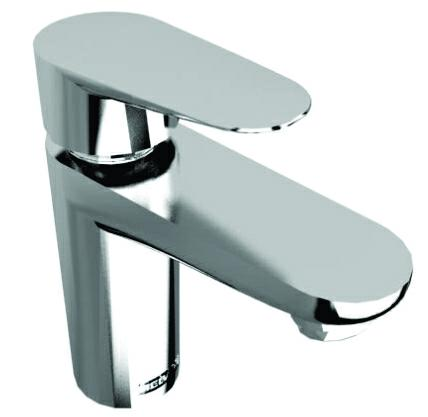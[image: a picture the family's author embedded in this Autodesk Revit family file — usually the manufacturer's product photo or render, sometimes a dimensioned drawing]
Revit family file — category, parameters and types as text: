
# Revit family: Monomando de Lavabo E918-1.9
name_source: partatom
category: Aparatos sanitarios
revit_build: Autodesk Revit 2016 (Build: 20150220_1215(x64)
units: mm (PartAtom-declared; Revit-internal decimal feet)

## family parameters
Compartido = Sí
Corte con vacíos al cargar = No
Cota de conector redondo = Diámetro de uso
Número OmniClass = 23.45.55.14
Punto de cálculo de habitación = Sí
Se basa en plano de trabajo = Sí
Siempre vertical = Sí
Tipo de pieza = Normal
Título OmniClass = Single Faucets

## types (1)
- E918-1.9
    Accesorios = Conectores ½ -14 NPSM
    Altura Total = 6"
    Anchura Total = 2"
    Características del Producto = Monomando tubular para lavabo.
    Cartucho = Cartucho Ø25 mm con vástago metálico.
    Chrome = Brass
    Comentarios de tipo = Monomando tubular para lavabo sin contra.
    Cuerpo de Latón = Brass
    Descripción = Monomando Century E918-1.9
    Elevación por defecto = 1"
    Fabricante = HELVEX S.A. de C.V.
    Garantía = El producto HELVEX está garantizado como libre de defectos en materiales y procesos de fabricación. El producto HELVEX está garantizado, en lo que se refiere a los acabados; por un periodo de 10 años en los acabados cromo y duravex, y por 2 años en acabados diferentes al cromo, a partir de la fecha de compra indicada en la factura.
    Imagen de tipo = E918-1.9.jpg
    Instalación = Conexión ½ - 14 NPSM
    Modelo = E918-1.9
    Operación = El maneral tienen una rotación horizontal para la función de agua caliente y fría; y vertical para abrir y cerrar el flujo de agua.
    Presión Máxima de Trabajo = 85.3 psi
    Presión Mínima de Trabajo = 5.6 psi
    Profundidad Total = 5"

## geometry (parser evidence)
native form markers: Sweep x3
no freeform markers — native parametric forms only
